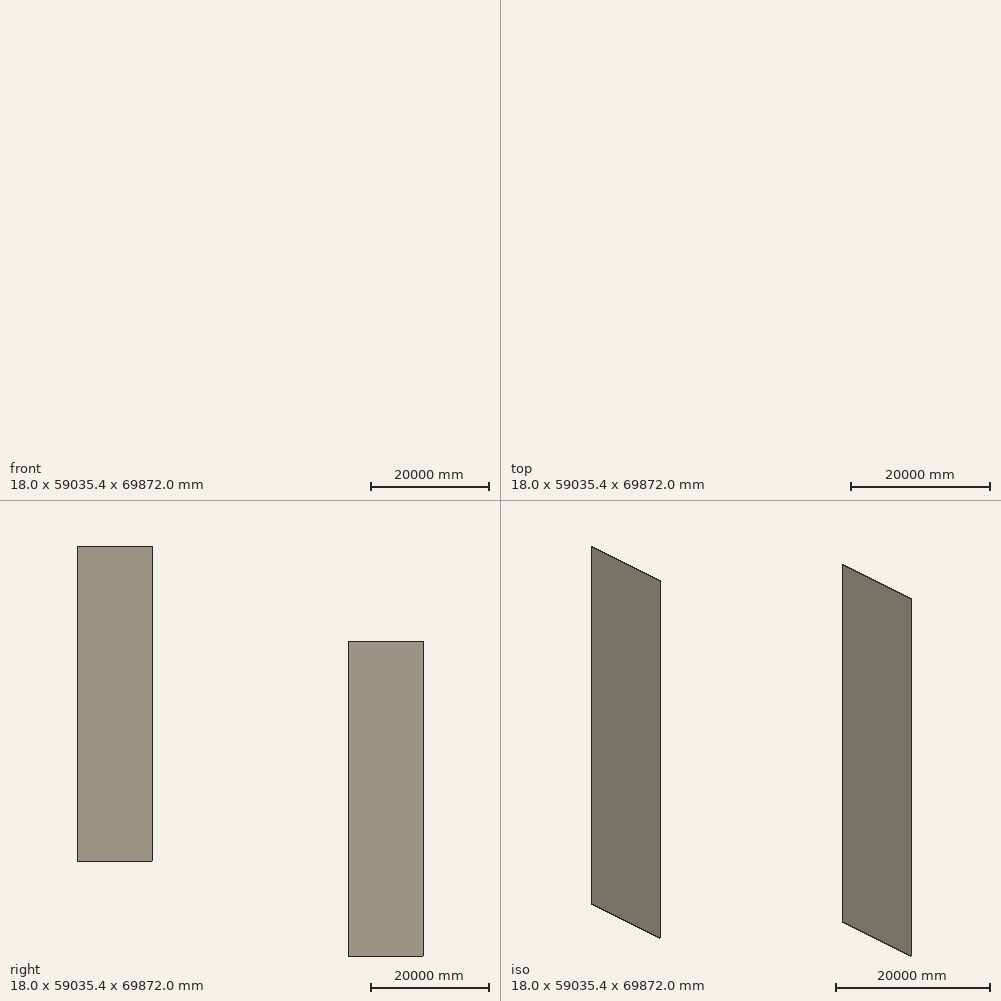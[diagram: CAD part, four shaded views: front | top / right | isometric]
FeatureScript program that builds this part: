
annotation { "Feature Type Name" : "Feature", "Feature Type Description" : "" }
export const myFeature = defineFeature(function(context is Context, id is Id, definition is map)
    precondition{}
    {
        {
            var Q0;
            Q0=qCreatedBy(makeId("Right.planeOp"),FACE);
            var sketch = newSketch(context, id + "F0", { "sketchPlane" : qUnion([Q0])});
            skLineSegment(sketch, "E0.bottom", {"start": v(-92591.77, 49030.56) * mm, "end": v(-105391.77, 49030.56) * mm});
            skLineSegment(sketch, "E0.top", {"start": v(-92591.77, -4676.17) * mm, "end": v(-105391.77, -4676.17) * mm});
            skLineSegment(sketch, "E0.left", {"start": v(-92591.77, 49030.56) * mm, "end": v(-92591.77, -4676.17) * mm});
            skLineSegment(sketch, "E0.right", {"start": v(-105391.77, 49030.56) * mm, "end": v(-105391.77, -4676.17) * mm});
            skSolve(sketch);
        }
        {
            var Q0;
            Q0=makeQuery(id+"F0.imprint","IMPRINT",FACE,{"disambiguationData":[TD([[makeQuery(id+"F0.imprint","IMPRINT",EDGE,{"derivedFrom":sQuery(id+"F0.wireOp",EDGE,"E0.bottom")}),1.0]])]});
            extrude(context, id + "F1", {"entities" : qUnion([Q0]), "depth" : 18 * mm});
        }
        {
            var Q0;
            Q0=qCreatedBy(makeId("Right.planeOp"),FACE);
            var sketch = newSketch(context, id + "F2", { "sketchPlane" : qUnion([Q0])});
            skLineSegment(sketch, "E1.bottom", {"start": v(-46356.36, 32865.24) * mm, "end": v(-59156.36, 32865.24) * mm});
            skLineSegment(sketch, "E1.top", {"start": v(-46356.36, -20841.48) * mm, "end": v(-59156.36, -20841.48) * mm});
            skLineSegment(sketch, "E1.left", {"start": v(-46356.36, 32865.24) * mm, "end": v(-46356.36, -20841.48) * mm});
            skLineSegment(sketch, "E1.right", {"start": v(-59156.36, 32865.24) * mm, "end": v(-59156.36, -20841.48) * mm});
            skSolve(sketch);
        }
        {
            var Q0;
            Q0=makeQuery(id+"F2.imprint","IMPRINT",FACE,{"disambiguationData":[TD([[makeQuery(id+"F2.imprint","IMPRINT",EDGE,{"derivedFrom":sQuery(id+"F2.wireOp",EDGE,"E1.bottom")}),1.0]])]});
            extrude(context, id + "F3", {"entities" : qUnion([Q0]), "depth" : 18 * mm});
        }
    });
